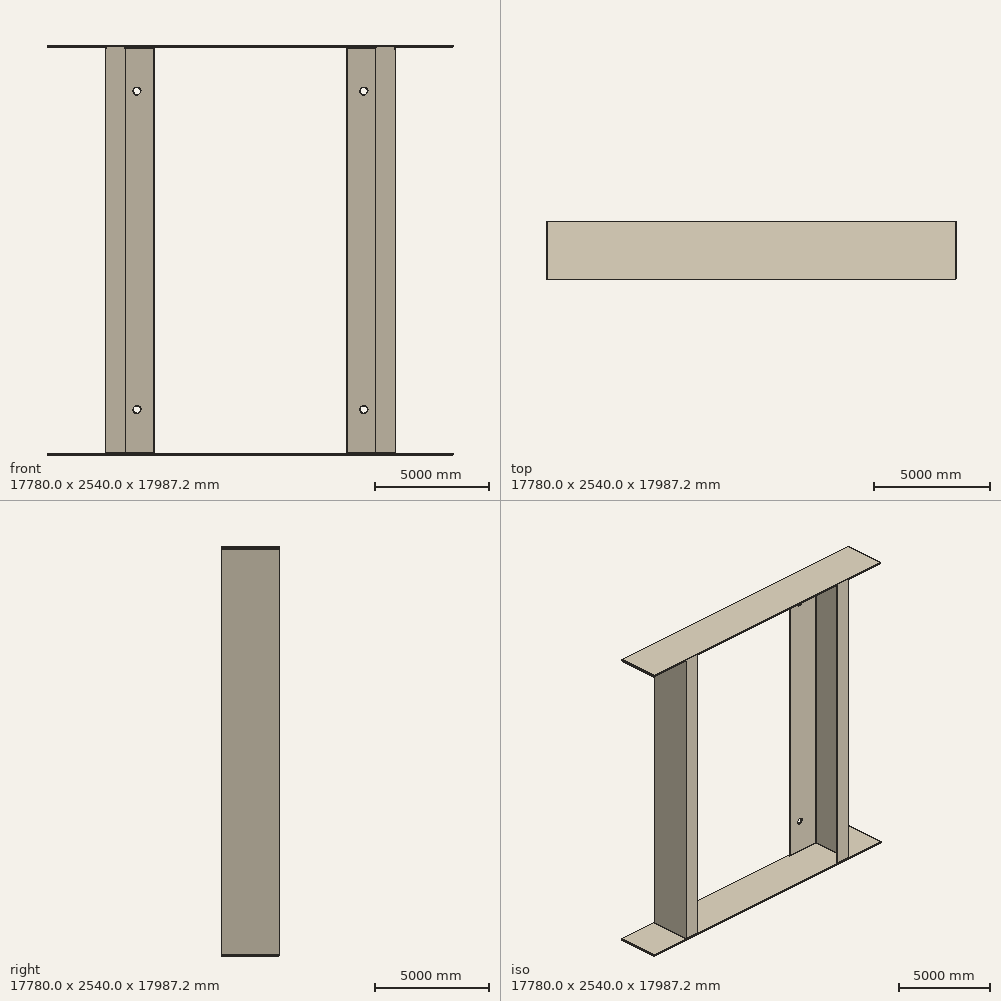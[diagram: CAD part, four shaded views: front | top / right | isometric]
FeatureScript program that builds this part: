
annotation { "Feature Type Name" : "Feature", "Feature Type Description" : "" }
export const myFeature = defineFeature(function(context is Context, id is Id, definition is map)
    precondition{}
    {
        {
            var Q0;
            Q0=qCreatedBy(makeId("Top.planeOp"),FACE);
            var sketch = newSketch(context, id + "F0", { "sketchPlane" : qUnion([Q0])});
            skLineSegment(sketch, "E0.bottom", {"start": v(8890, 1270) * mm, "end": v(-8890, 1270) * mm});
            skLineSegment(sketch, "E0.top", {"start": v(8890, -1270) * mm, "end": v(-8890, -1270) * mm});
            skLineSegment(sketch, "E0.left", {"start": v(8890, 1270) * mm, "end": v(8890, -1270) * mm});
            skLineSegment(sketch, "E0.right", {"start": v(-8890, 1270) * mm, "end": v(-8890, -1270) * mm});
            skPoint(sketch, "E0.middle", {"position": v(0, 0) * mm});
            skSolve(sketch);
        }
        {
            var Q0;
            Q0 = qSketchRegion(id + "F0", true);
            extrude(context, id + "F1", {"entities" : qUnion([Q0]), "depth" : 4 * mm, "offsetDistance" : 25.4 * mm});
        }
        {
            var Q0;
            Q0=makeQuery(id+"F1.opExtrude","CAP_FACE",FACE,{"disambiguationData":[OSD([sQuery(id+"F0.wireOp",EDGE,"E0.bottom"),sQuery(id+"F0.wireOp",EDGE,"E0.top"),sQuery(id+"F0.wireOp",EDGE,"E0.left"),sQuery(id+"F0.wireOp",EDGE,"E0.right")])],"isStart":false});
            var sketch = newSketch(context, id + "F2", { "sketchPlane" : qUnion([Q0])});
            skLineSegment(sketch, "E1.bottom", {"start": v(-6350, 1270) * mm, "end": v(-6248.4, 1270) * mm});
            skLineSegment(sketch, "E1.top", {"start": v(-6350, -1270) * mm, "end": v(-6248.4, -1270) * mm});
            skLineSegment(sketch, "E1.left", {"start": v(-6350, 1270) * mm, "end": v(-6350, -1270) * mm});
            skLineSegment(sketch, "E1.right", {"start": v(-6248.4, 1270) * mm, "end": v(-6248.4, -1270) * mm});
            skLineSegment(sketch, "E2.bottom", {"start": v(-6248.4, -1270) * mm, "end": v(-5486.4, -1270) * mm});
            skLineSegment(sketch, "E2.top", {"start": v(-6248.4, -1168.4) * mm, "end": v(-5486.4, -1168.4) * mm});
            skLineSegment(sketch, "E2.left", {"start": v(-6248.4, -1270) * mm, "end": v(-6248.4, -1168.4) * mm});
            skLineSegment(sketch, "E2.right", {"start": v(-5486.4, -1270) * mm, "end": v(-5486.4, -1168.4) * mm});
            skLineSegment(sketch, "E3.bottom", {"start": v(-6248.4, 1270) * mm, "end": v(-4216.4, 1270) * mm});
            skLineSegment(sketch, "E3.top", {"start": v(-6248.4, 1168.4) * mm, "end": v(-4216.4, 1168.4) * mm});
            skLineSegment(sketch, "E3.left", {"start": v(-6248.4, 1270) * mm, "end": v(-6248.4, 1168.4) * mm});
            skLineSegment(sketch, "E3.right", {"start": v(-4216.4, 1270) * mm, "end": v(-4216.4, 1168.4) * mm});
            skLineSegment(sketch, "E4.MirrorCS", {"start": v(4216.4, 1270) * mm, "end": v(4216.4, 1168.4) * mm});
            skLineSegment(sketch, "E5.MirrorCS", {"start": v(6350, -1270) * mm, "end": v(6248.4, -1270) * mm});
            skLineSegment(sketch, "E6.MirrorCS", {"start": v(6248.4, 1270) * mm, "end": v(6248.4, -1270) * mm});
            skLineSegment(sketch, "E7.MirrorCS", {"start": v(6248.4, -1168.4) * mm, "end": v(5486.4, -1168.4) * mm});
            skLineSegment(sketch, "E8.MirrorCS", {"start": v(6248.4, 1270) * mm, "end": v(4216.4, 1270) * mm});
            skLineSegment(sketch, "E9.MirrorCS", {"start": v(6248.4, 1270) * mm, "end": v(6248.4, 1168.4) * mm});
            skLineSegment(sketch, "E10.MirrorCS", {"start": v(6350, 1270) * mm, "end": v(6248.4, 1270) * mm});
            skLineSegment(sketch, "E11.MirrorCS", {"start": v(6350, 1270) * mm, "end": v(6350, -1270) * mm});
            skLineSegment(sketch, "E12.MirrorCS", {"start": v(6248.4, -1270) * mm, "end": v(5486.4, -1270) * mm});
            skLineSegment(sketch, "E13.MirrorCS", {"start": v(6248.4, -1270) * mm, "end": v(6248.4, -1168.4) * mm});
            skLineSegment(sketch, "E14.MirrorCS", {"start": v(5486.4, -1270) * mm, "end": v(5486.4, -1168.4) * mm});
            skLineSegment(sketch, "E15.MirrorCS", {"start": v(6248.4, 1168.4) * mm, "end": v(4216.4, 1168.4) * mm});
            skPoint(sketch, "E16.start.orphan", {"position": v(0, 7299.84) * mm});
            skSolve(sketch);
        }
        {
            var Q0;
            Q0=makeQuery(id+"F2.imprint","IMPRINT",FACE,{"disambiguationData":[TD([[makeQuery(id+"F2.imprint","IMPRINT",EDGE,{"derivedFrom":sQuery(id+"F2.wireOp",EDGE,"E1.bottom")}),1.0]])]});
            var Q1;
            Q1=makeQuery(id+"F2.imprint","IMPRINT",FACE,{"disambiguationData":[TD([[makeQuery(id+"F2.imprint","IMPRINT",EDGE,{"derivedFrom":sQuery(id+"F2.wireOp",EDGE,"E2.bottom")}),-1.0]])]});
            var Q2;
            Q2=makeQuery(id+"F2.imprint","IMPRINT",FACE,{"disambiguationData":[TD([[makeQuery(id+"F2.imprint","IMPRINT",EDGE,{"derivedFrom":sQuery(id+"F2.wireOp",EDGE,"E3.bottom")}),1.0]])]});
            var Q3;
            Q3=makeQuery(id+"F2.imprint","IMPRINT",FACE,{"disambiguationData":[TD([[makeQuery(id+"F2.imprint","IMPRINT",EDGE,{"derivedFrom":sQuery(id+"F2.wireOp",EDGE,"E5.MirrorCS")}),-1.0]])]});
            var Q4;
            Q4=makeQuery(id+"F2.imprint","IMPRINT",FACE,{"disambiguationData":[TD([[makeQuery(id+"F2.imprint","IMPRINT",EDGE,{"derivedFrom":sQuery(id+"F2.wireOp",EDGE,"E7.MirrorCS")}),1.0]])]});
            var Q5;
            Q5=makeQuery(id+"F2.imprint","IMPRINT",FACE,{"disambiguationData":[TD([[makeQuery(id+"F2.imprint","IMPRINT",EDGE,{"derivedFrom":sQuery(id+"F2.wireOp",EDGE,"E4.MirrorCS")}),1.0]])]});
            extrude(context, id + "F3", {"entities" : qUnion([Q0, Q1, Q2, Q3, Q4, Q5]), "operationType" : NewBodyOperationType.ADD, "depth" : 17780 * mm, "offsetDistance" : 25.4 * mm});
        }
        {
            var Q0;
            Q0=makeQuery(id+"F3.opExtrude","SWEPT_FACE",FACE,{"disambiguationData":[OSD([sQuery(id+"F2.wireOp",EDGE,"E3.top")])]});
            var sketch = newSketch(context, id + "F4", { "sketchPlane" : qUnion([Q0])});
            skCircle(sketch, "E17", {"center": v(-4978.4, 15879) * mm, "radius": 152.4 * mm});
            skCircle(sketch, "E18", {"center": v(-4978.4, 1909) * mm, "radius": 152.4 * mm});
            skCircle(sketch, "E19", {"center": v(4978.4, 15879) * mm, "radius": 152.4 * mm});
            skCircle(sketch, "E20", {"center": v(4978.4, 1909) * mm, "radius": 152.4 * mm});
            skSolve(sketch);
        }
        {
            var Q0;
            Q0 = qSketchRegion(id + "F4", true);
            extrude(context, id + "F5", {"entities" : qUnion([Q0]), "operationType" : NewBodyOperationType.REMOVE, "oppositeDirection" : true, "depth" : 854.57 * mm, "offsetDistance" : 25.4 * mm});
        }
        {
            var Q0;
            Q0=makeQuery(id+"F3.opExtrude","CAP_FACE",FACE,{"disambiguationData":[OSD([sQuery(id+"F2.wireOp",EDGE,"E1.bottom"),sQuery(id+"F2.wireOp",EDGE,"E1.top"),sQuery(id+"F2.wireOp",EDGE,"E1.left"),sQuery(id+"F2.wireOp",EDGE,"E1.right"),sQuery(id+"F2.wireOp",EDGE,"E2.bottom"),sQuery(id+"F2.wireOp",EDGE,"E2.top"),sQuery(id+"F2.wireOp",EDGE,"E2.right"),sQuery(id+"F2.wireOp",EDGE,"E3.bottom"),sQuery(id+"F2.wireOp",EDGE,"E3.top"),sQuery(id+"F2.wireOp",EDGE,"E3.right")])],"isStart":false});
            var sketch = newSketch(context, id + "F6", { "sketchPlane" : qUnion([Q0])});
            skLineSegment(sketch, "E21.bottom", {"start": v(-8890, -1270) * mm, "end": v(8890, -1270) * mm});
            skLineSegment(sketch, "E21.top", {"start": v(-8890, 1270) * mm, "end": v(8890, 1270) * mm});
            skLineSegment(sketch, "E21.left", {"start": v(-6350, -1270) * mm, "end": v(-6350, 1270) * mm});
            skLineSegment(sketch, "E21.right", {"start": v(8890, -1270) * mm, "end": v(8890, 1270) * mm});
            skLineSegment(sketch, "E22", {"start": v(-8890, -1270) * mm, "end": v(-8890, 1270) * mm});
            skSolve(sketch);
        }
        {
            var Q0;
            Q0 = qSketchRegion(id + "F6", true);
            extrude(context, id + "F7", {"entities" : qUnion([Q0]), "operationType" : NewBodyOperationType.ADD, "depth" : 101.6 * mm, "offsetDistance" : 25.4 * mm});
        }
        {
            var Q0;
            Q0=makeQuery(id+"F7.opExtrude","CAP_EDGE",EDGE,{"disambiguationData":[OSD([sQuery(id+"F6.wireOp",EDGE,"E21.bottom")])],"isStart":false});
            fillet(context, id + "F8", {"entities" : qUnion([Q0]), "radius" : 25.4 * mm, "tangentPropagation" : true, "allowEdgeOverflow" : false});
        }
        {
            var Q0;
            Q0=makeQuery(id+"F7.opExtrude","CAP_FACE",FACE,{"disambiguationData":[OSD([sQuery(id+"F6.wireOp",EDGE,"E21.bottom"),sQuery(id+"F6.wireOp",EDGE,"E21.top"),sQuery(id+"F6.wireOp",EDGE,"E21.right"),sQuery(id+"F6.wireOp",EDGE,"E22")])],"isStart":false});
            fillet(context, id + "F9", {"entities" : qUnion([Q0]), "radius" : 25.4 * mm, "tangentPropagation" : true, "allowEdgeOverflow" : false});
        }
        {
            var Q0;
            {var subQ0=sQuery(id+"F6.wireOp",EDGE,"E21.top");var subQ1=sQuery(id+"F6.wireOp",EDGE,"E21.bottom");var subQ2=sQuery(id+"F6.wireOp",EDGE,"E22");Q0=makeQuery(id+"F7.boolean.opBoolean","SPLIT",FACE,{"disambiguationData":[TD([makeQuery(id+"F3.opExtrude","SWEPT_FACE",FACE,{"disambiguationData":[OSD([sQuery(id+"F2.wireOp",EDGE,"E1.left")])]})])],"derivedFrom":makeQuery(id+"F7.opExtrude","CAP_FACE",FACE,{"disambiguationData":[OSD([subQ1,subQ0,sQuery(id+"F6.wireOp",EDGE,"E21.right"),subQ2])],"isStart":true})});}
            fillet(context, id + "F10", {"entities" : qUnion([Q0]), "radius" : 25.4 * mm, "tangentPropagation" : true, "allowEdgeOverflow" : false});
        }
        {
            var Q0;
            {var subQ0=sQuery(id+"F6.wireOp",EDGE,"E21.right");var subQ1=sQuery(id+"F6.wireOp",EDGE,"E21.top");var subQ2=sQuery(id+"F6.wireOp",EDGE,"E21.bottom");Q0=makeQuery(id+"F7.boolean.opBoolean","SPLIT",FACE,{"disambiguationData":[TD([makeQuery(id+"F3.opExtrude","SWEPT_FACE",FACE,{"disambiguationData":[OSD([sQuery(id+"F2.wireOp",EDGE,"E11.MirrorCS")])]})])],"derivedFrom":makeQuery(id+"F7.opExtrude","CAP_FACE",FACE,{"disambiguationData":[OSD([subQ2,subQ1,subQ0,sQuery(id+"F6.wireOp",EDGE,"E22")])],"isStart":true})});}
            var Q1;
            {var subQ0=sQuery(id+"F6.wireOp",EDGE,"E21.top");var subQ1=sQuery(id+"F6.wireOp",EDGE,"E21.bottom");Q1=makeQuery(id+"F7.boolean.opBoolean","SPLIT",FACE,{"disambiguationData":[TD([makeQuery(id+"F3.opExtrude","SWEPT_FACE",FACE,{"disambiguationData":[OSD([sQuery(id+"F2.wireOp",EDGE,"E1.right")])]})])],"derivedFrom":makeQuery(id+"F7.opExtrude","CAP_FACE",FACE,{"disambiguationData":[OSD([subQ1,subQ0,sQuery(id+"F6.wireOp",EDGE,"E21.right"),sQuery(id+"F6.wireOp",EDGE,"E22")])],"isStart":true})});}
            fillet(context, id + "F11", {"entities" : qUnion([Q0, Q1]), "radius" : 25.4 * mm, "tangentPropagation" : true, "allowEdgeOverflow" : false});
        }
        {
            var Q0;
            Q0=makeQuery(id+"F1.opExtrude","CAP_FACE",FACE,{"disambiguationData":[OSD([sQuery(id+"F0.wireOp",EDGE,"E0.bottom"),sQuery(id+"F0.wireOp",EDGE,"E0.top"),sQuery(id+"F0.wireOp",EDGE,"E0.left"),sQuery(id+"F0.wireOp",EDGE,"E0.right")])],"isStart":true});
            fillet(context, id + "F12", {"entities" : qUnion([Q0]), "radius" : 25.4 * mm, "tangentPropagation" : true, "allowEdgeOverflow" : false});
        }
        {
            var Q0;
            Q0=makeQuery(id+"F0.imprint","IMPRINT",FACE,{"disambiguationData":[TD([[makeQuery(id+"F0.imprint","IMPRINT",EDGE,{"derivedFrom":sQuery(id+"F0.wireOp",EDGE,"E0.bottom")}),1.0]])]});
            extrude(context, id + "F13", {"entities" : qUnion([Q0]), "operationType" : NewBodyOperationType.ADD, "oppositeDirection" : true, "depth" : 101.6 * mm, "offsetDistance" : 25.4 * mm});
        }
        {
            var Q0;
            Q0=makeQuery(id+"F13.opExtrude","CAP_FACE",FACE,{"disambiguationData":[OSD([sQuery(id+"F0.wireOp",EDGE,"E0.bottom"),sQuery(id+"F0.wireOp",EDGE,"E0.top"),sQuery(id+"F0.wireOp",EDGE,"E0.left"),sQuery(id+"F0.wireOp",EDGE,"E0.right")])],"isStart":false});
            fillet(context, id + "F14", {"entities" : qUnion([Q0]), "radius" : 25.4 * mm, "tangentPropagation" : true, "allowEdgeOverflow" : false});
        }
        {
            var Q0;
            Q0=makeQuery(id+"F3.opExtrude","SWEPT_FACE",FACE,{"disambiguationData":[OSD([sQuery(id+"F2.wireOp",EDGE,"E15.MirrorCS")])]});
            fillet(context, id + "F15", {"entities" : qUnion([Q0]), "radius" : 25.4 * mm, "tangentPropagation" : true, "allowEdgeOverflow" : false});
        }
        {
            var Q0;
            Q0=makeQuery(id+"F3.opExtrude","SWEPT_FACE",FACE,{"disambiguationData":[OSD([sQuery(id+"F2.wireOp",EDGE,"E3.top")])]});
            fillet(context, id + "F16", {"entities" : qUnion([Q0]), "radius" : 25.4 * mm, "tangentPropagation" : true, "allowEdgeOverflow" : false});
        }
        {
            var Q0;
            Q0=makeQuery(id+"F5.boolean.opBoolean","INTERSECT",EDGE,{"derivedFrom":[makeQuery(id+"F3.boolean.opBoolean","MERGE",FACE,{"derivedFrom":[makeQuery(id+"F1.opExtrude","SWEPT_FACE",FACE,{"disambiguationData":[OSD([sQuery(id+"F0.wireOp",EDGE,"E0.bottom")])]}),makeQuery(id+"F3.opExtrude","SWEPT_FACE",FACE,{"disambiguationData":[OSD([sQuery(id+"F2.wireOp",EDGE,"E1.bottom"),sQuery(id+"F2.wireOp",EDGE,"E3.bottom")])]}),makeQuery(id+"F3.opExtrude","SWEPT_FACE",FACE,{"disambiguationData":[OSD([sQuery(id+"F2.wireOp",EDGE,"E8.MirrorCS"),sQuery(id+"F2.wireOp",EDGE,"E10.MirrorCS")])]})]}),makeQuery(id+"F5.opExtrude","SWEPT_FACE",FACE,{"disambiguationData":[OSD([sQuery(id+"F4.wireOp",EDGE,"E17")])]})]});
            fillet(context, id + "F17", {"entities" : qUnion([Q0]), "radius" : 25.4 * mm, "tangentPropagation" : true, "allowEdgeOverflow" : false});
        }
        {
            var Q0;
            Q0=makeQuery(id+"F5.boolean.opBoolean","INTERSECT",EDGE,{"derivedFrom":[makeQuery(id+"F3.boolean.opBoolean","MERGE",FACE,{"derivedFrom":[makeQuery(id+"F1.opExtrude","SWEPT_FACE",FACE,{"disambiguationData":[OSD([sQuery(id+"F0.wireOp",EDGE,"E0.bottom")])]}),makeQuery(id+"F3.opExtrude","SWEPT_FACE",FACE,{"disambiguationData":[OSD([sQuery(id+"F2.wireOp",EDGE,"E1.bottom"),sQuery(id+"F2.wireOp",EDGE,"E3.bottom")])]}),makeQuery(id+"F3.opExtrude","SWEPT_FACE",FACE,{"disambiguationData":[OSD([sQuery(id+"F2.wireOp",EDGE,"E8.MirrorCS"),sQuery(id+"F2.wireOp",EDGE,"E10.MirrorCS")])]})]}),makeQuery(id+"F5.opExtrude","SWEPT_FACE",FACE,{"disambiguationData":[OSD([sQuery(id+"F4.wireOp",EDGE,"E18")])]})]});
            fillet(context, id + "F18", {"entities" : qUnion([Q0]), "radius" : 25.4 * mm, "tangentPropagation" : true, "allowEdgeOverflow" : false});
        }
        {
            var Q0;
            Q0=makeQuery(id+"F5.boolean.opBoolean","INTERSECT",EDGE,{"derivedFrom":[makeQuery(id+"F3.boolean.opBoolean","MERGE",FACE,{"derivedFrom":[makeQuery(id+"F1.opExtrude","SWEPT_FACE",FACE,{"disambiguationData":[OSD([sQuery(id+"F0.wireOp",EDGE,"E0.bottom")])]}),makeQuery(id+"F3.opExtrude","SWEPT_FACE",FACE,{"disambiguationData":[OSD([sQuery(id+"F2.wireOp",EDGE,"E1.bottom"),sQuery(id+"F2.wireOp",EDGE,"E3.bottom")])]}),makeQuery(id+"F3.opExtrude","SWEPT_FACE",FACE,{"disambiguationData":[OSD([sQuery(id+"F2.wireOp",EDGE,"E8.MirrorCS"),sQuery(id+"F2.wireOp",EDGE,"E10.MirrorCS")])]})]}),makeQuery(id+"F5.opExtrude","SWEPT_FACE",FACE,{"disambiguationData":[OSD([sQuery(id+"F4.wireOp",EDGE,"E20")])]})]});
            var Q1;
            Q1=makeQuery(id+"F5.boolean.opBoolean","INTERSECT",EDGE,{"derivedFrom":[makeQuery(id+"F3.boolean.opBoolean","MERGE",FACE,{"derivedFrom":[makeQuery(id+"F1.opExtrude","SWEPT_FACE",FACE,{"disambiguationData":[OSD([sQuery(id+"F0.wireOp",EDGE,"E0.bottom")])]}),makeQuery(id+"F3.opExtrude","SWEPT_FACE",FACE,{"disambiguationData":[OSD([sQuery(id+"F2.wireOp",EDGE,"E1.bottom"),sQuery(id+"F2.wireOp",EDGE,"E3.bottom")])]}),makeQuery(id+"F3.opExtrude","SWEPT_FACE",FACE,{"disambiguationData":[OSD([sQuery(id+"F2.wireOp",EDGE,"E8.MirrorCS"),sQuery(id+"F2.wireOp",EDGE,"E10.MirrorCS")])]})]}),makeQuery(id+"F5.opExtrude","SWEPT_FACE",FACE,{"disambiguationData":[OSD([sQuery(id+"F4.wireOp",EDGE,"E19")])]})]});
            fillet(context, id + "F19", {"entities" : qUnion([Q0, Q1]), "radius" : 25.4 * mm, "tangentPropagation" : true, "allowEdgeOverflow" : false});
        }
    });
